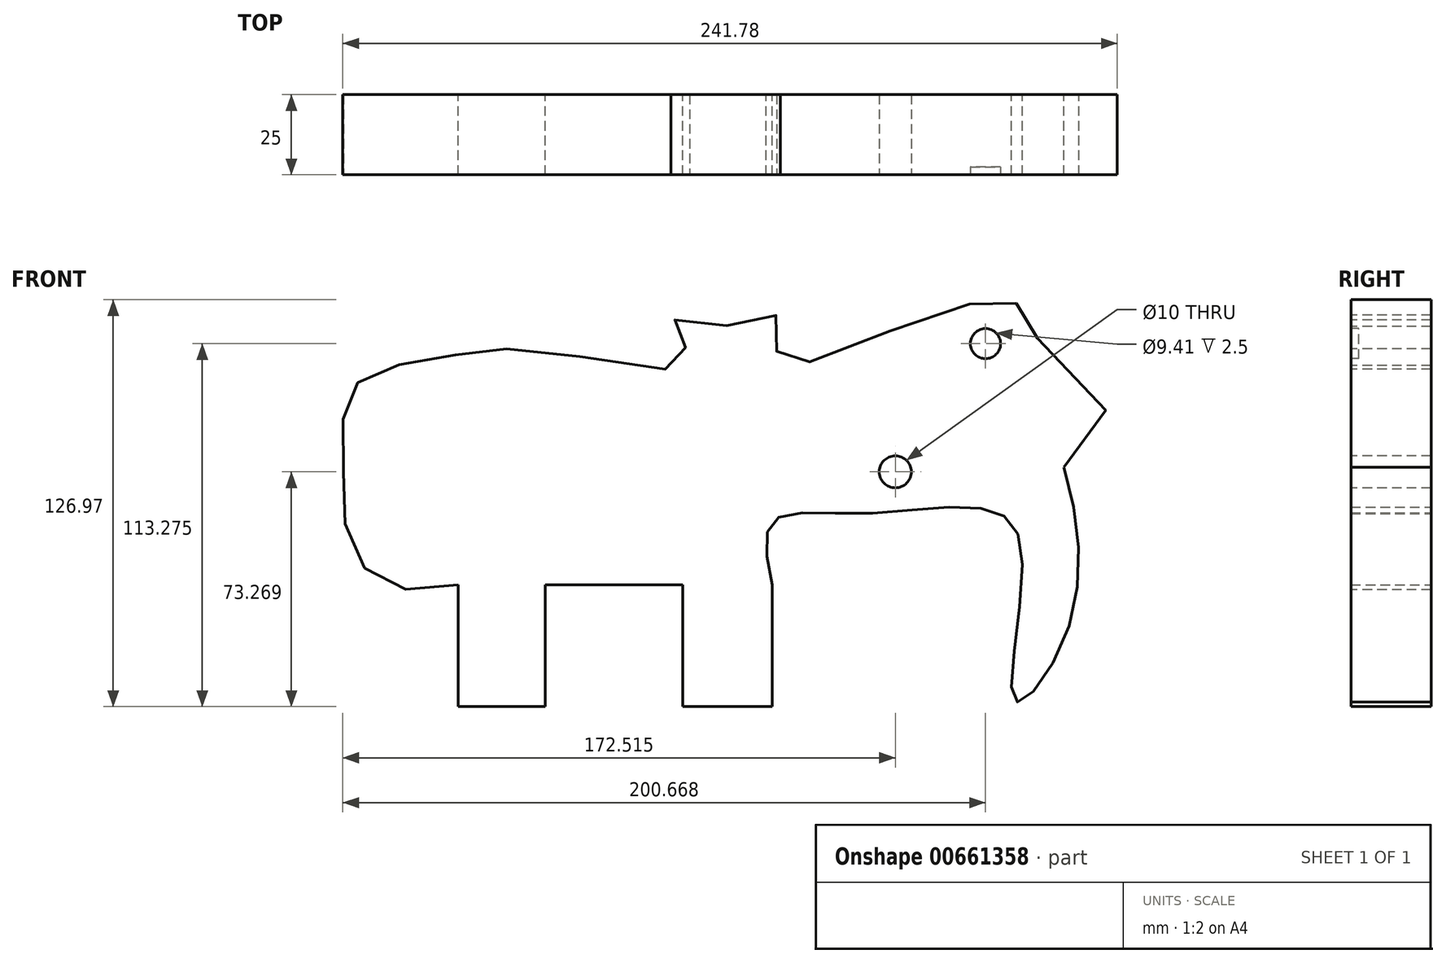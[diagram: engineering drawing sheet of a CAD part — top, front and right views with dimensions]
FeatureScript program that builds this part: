
annotation { "Feature Type Name" : "Feature", "Feature Type Description" : "" }
export const myFeature = defineFeature(function(context is Context, id is Id, definition is map)
    precondition{}
    {
        {
            var Q0;
            Q0=qCreatedBy(makeId("Front.planeOp"),FACE);
            var sketch = newSketch(context, id + "F0", { "sketchPlane" : qUnion([Q0])});
            skLineSegment(sketch, "E0", {"start": v(-66.44, -31.13) * mm, "end": v(-66.44, 6.87) * mm});
            skLineSegment(sketch, "E1", {"start": v(-66.44, 6.87) * mm, "end": v(-23.48, 6.87) * mm});
            skLineSegment(sketch, "E2", {"start": v(-23.48, 6.87) * mm, "end": v(-23.48, -31.13) * mm});
            skLineSegment(sketch, "E3", {"start": v(-23.48, -31.13) * mm, "end": v(4.5, -31.13) * mm});
            skLineSegment(sketch, "E4", {"start": v(4.5, -31.13) * mm, "end": v(4.5, 6.87) * mm});
            skLineSegment(sketch, "E5", {"start": v(-66.44, -31.13) * mm, "end": v(-93.55, -31.13) * mm});
            skLineSegment(sketch, "E6", {"start": v(-93.55, -31.13) * mm, "end": v(-93.55, 6.87) * mm});
            skFitSpline(sketch, "E7", {"points": [v(-93.55, 6.87) * mm, v(-115.74, 6.87) * mm, v(-127.82, 21.3) * mm, v(-129.42, 44) * mm, v(-128.33, 64.97) * mm, v(-119.12, 73.4) * mm, v(-93.55, 78.72) * mm, v(-65.38, 79.7) * mm, v(-21.41, 76.4) * mm, v(-27.15, 88.93) * mm, v(-12.44, 87.52) * mm, v(6.67, 90.29) * mm, v(6.36, 76.88) * mm, v(45.45, 87.77) * mm, v(80.07, 95.1) * mm, v(90.05, 80.46) * mm, v(95.54, 43.54) * mm], "startDerivative": vector(-389.68, -65.1) * mm, "endDerivative": vector(-1326.9, -173.24) * mm});
            skFitSpline(sketch, "E8", {"points": [v(4.5, 6.87) * mm, v(4.5, 26.52) * mm, v(31.5, 29.12) * mm, v(72.83, 30.1) * mm, v(82.6, 14.16) * mm, v(80.31, -29.45) * mm, v(96.26, -8.62) * mm, v(95.54, 43.54) * mm], "startDerivative": vector(-44.25, 208.65) * mm, "endDerivative": vector(-81.57, 285.3) * mm});
            skSolve(sketch);
        }
        {
            var Q0;
            Q0 = qSketchRegion(id + "F0", true);
            extrude(context, id + "F1", {"entities" : qUnion([Q0]), "depth" : 25 * mm, "offsetDistance" : 25 * mm});
        }
        {
            var Q0;
            Q0=makeQuery(id+"F1.opExtrude","CAP_FACE",FACE,{"disambiguationData":[OSD([sQuery(id+"F0.wireOp",EDGE,"E0"),sQuery(id+"F0.wireOp",EDGE,"E1"),sQuery(id+"F0.wireOp",EDGE,"E2"),sQuery(id+"F0.wireOp",EDGE,"E3"),sQuery(id+"F0.wireOp",EDGE,"E4"),sQuery(id+"F0.wireOp",EDGE,"E5"),sQuery(id+"F0.wireOp",EDGE,"E6"),sQuery(id+"F0.wireOp",EDGE,"E7"),sQuery(id+"F0.wireOp",EDGE,"E8")])],"isStart":false});
            var sketch = newSketch(context, id + "F2", { "sketchPlane" : qUnion([Q0])});
            skCircle(sketch, "E9", {"center": v(42.9, 42.14) * mm, "radius": 5 * mm});
            skSolve(sketch);
        }
        {
            var Q0;
            Q0 = qSketchRegion(id + "F2", true);
            extrude(context, id + "F3", {"entities" : qUnion([Q0]), "operationType" : NewBodyOperationType.REMOVE, "oppositeDirection" : true, "depth" : 25 * mm, "offsetDistance" : 25 * mm});
        }
        {
            var Q0;
            Q0=makeQuery(id+"F1.opExtrude","CAP_FACE",FACE,{"disambiguationData":[OSD([sQuery(id+"F0.wireOp",EDGE,"E0"),sQuery(id+"F0.wireOp",EDGE,"E1"),sQuery(id+"F0.wireOp",EDGE,"E2"),sQuery(id+"F0.wireOp",EDGE,"E3"),sQuery(id+"F0.wireOp",EDGE,"E4"),sQuery(id+"F0.wireOp",EDGE,"E5"),sQuery(id+"F0.wireOp",EDGE,"E6"),sQuery(id+"F0.wireOp",EDGE,"E7"),sQuery(id+"F0.wireOp",EDGE,"E8")])],"isStart":false});
            var sketch = newSketch(context, id + "F4", { "sketchPlane" : qUnion([Q0])});
            skCircle(sketch, "E10", {"center": v(71.05, 82.14) * mm, "radius": 4.7 * mm});
            skSolve(sketch);
        }
        {
            var Q0;
            Q0 = qSketchRegion(id + "F4", true);
            extrude(context, id + "F5", {"entities" : qUnion([Q0]), "operationType" : NewBodyOperationType.REMOVE, "endBound" : BoundingType.SYMMETRIC, "oppositeDirection" : true, "depth" : 5 * mm, "offsetDistance" : 25 * mm});
        }
    });
